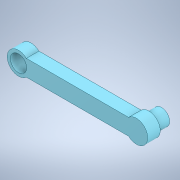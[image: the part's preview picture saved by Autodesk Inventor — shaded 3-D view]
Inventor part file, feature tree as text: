
AUTODESK INVENTOR PART (.ipt)
format: ipt  version: 2022 (Build 260153000, 153)  size: 128,000 bytes
history: native  units: in
note: dims shown in document units (in); Inventor stores cm internally (conversion verified against a paired STEP export)
features: extrude x2, sketch x1
ambient origin geometry x8: Origin, YZ Plane, XZ Plane, XY Plane, X Axis, Y Axis, Z Axis, Center Point
bodies: Solid1 (feature_tree)
feature tree (3):
  sketch  "Sketch2"  dims[d0=0.1969in d1=0.0in d2=0.1969in d3=0.0in d4=1.8504in d6=1.378in d8=0.2559in d10=0.3543in d11=0.2559in]
  extrude  "Extrusion1"  TaperAngle=0.0deg  [1 undecoded]
  extrude  "Extrusion2"  Depth=0.1969in
note: 1 required parameter value undecoded (feature->parameter linkage not recoverable at this tier; creation-order binding heuristic only, values carry confidence <= 0.55)
